# Revit family: Scale-SR_Scales-SR7005i
name_source: partatom
category: Specialty Equipment
units: mm (PartAtom-declared; Revit-internal decimal feet)

## family parameters
Always vertical = Yes
Cut with Voids When Loaded = No
OmniClass Number = 23.40.70.11.14.11
OmniClass Title = Medical Equipment
Part Type = Normal
Room Calculation Point = No
Round Connector Dimension = Use Diameter
Shared = No
Work Plane-Based = No

## types (2) — shared parameters
Assembly Code = E1020810
Auto Power Down = 30 to 300 Seconds
Auto Zero = Fold Unit Down or Press Button
Averaging = Automatic Digital Filter
BIM Version = v3.1
BIM Version Available (Earliest) = 2017
Calibration = Traceable to NIST Standards
Default Elevation = 0"
Display Resolution = 0.1 lb / 0.1 kg
Display Type = 16-Character Dot-Matrix LCD
Housing Depth = 3 1/4"
Housing Height = 31 1/2"
Housing Width = 26"
Manufacturer = SR Scales by SR Instruments, Inc.
Maximum Weight Capacity = 660 lbs or 300 kg
Optional Accessories Note = Height Rod and Printer Kit Options are Not Modeled in Family - for Specifying only
Optional Height Rod Part Number = SR8591
Optional Printer Kit Part Number = SR8327
Optional Remote Printer Kit = Yes
Optional Wall Mounted Height Rod = Yes
Platform Depth = 20"
Platform Size = 18'' x 20'' (45.8 cm x 50.8 cm)
Platform Width = 18 3/8"
Power Supply = Six (6) ''C'' Cell Batteries, Medical Grade AC Power Supply
Product Page URL = https://srinstruments.com
Projection From Wall Folded Down = 24"
URL = http://www.srinstruments.com

## per-type parameters (varying)
| type | Description |
| SR7005i | 18" x 20" Wall Mount In-Room Mini Scale |
| SR7005i-KG | 18" x 20" Wall Mount In-Room Mini Scale - KG Only |

note: column(s) folded — value = type name in every type: Model

## geometry (parser evidence)
native form markers: Sweep x1
no freeform markers — native parametric forms only
